# Revit family: Accessory-Flush_Actuator_Plate-KOHLER-DROPLET-K-4177IN_1
name_source: partatom
category: Specialty Equipment
revit_build: Autodesk Revit 2017 (Build: 20160225_1515(x64)
units: mm (PartAtom-declared; Revit-internal decimal feet)

## family parameters
Cut with Voids When Loaded = No
Host = Face
OmniClass Number = 23.31.25.00
OmniClass Title = Toilet and Bath Specialties
Part Type = Normal
Room Calculation Point = No
Round Connector Dimension = Use Diameter
Shared = No

## types (1)
- CP-Polished Chrome
    ADA Compliant = No
    Assembly Code = C1030200
    Date Modified = 01/05/2020
    Default Elevation = 42"
    Description = Face Plate for Inwall Tank
    Finish = Kohler-Plastic-CP-Polished_Chrome
    Height = 6 5/16"
    Length = 3/8"
    Manufacturer = KOHLER Co.
    Master Format 2014 = 10 28 00
    Master Format 2014 Name = Toilet, Bath, and Laundry Accessories
    Material = Plastic
    Model = K-4177IN-M-CP
    Product Documentation Link = http://resources.kohler.com
    Product Name = DROPLET
    Product Page URL = https://www.kohler.co.in
    Type = 1
    URL = https://www.kohler.co.in
    WaterSense Certified = No
    Width = 8 7/8"

## geometry (parser evidence)
native form markers: Sweep x3
no freeform markers — native parametric forms only
